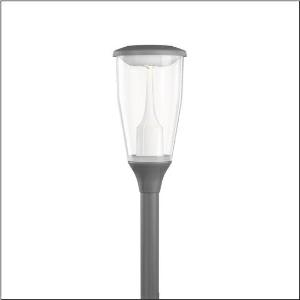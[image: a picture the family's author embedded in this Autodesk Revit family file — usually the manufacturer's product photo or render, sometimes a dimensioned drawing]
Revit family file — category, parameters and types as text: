
# Revit family: dl_11_iq___p1_0a_5xa5575bf14h000022_7e97
name_source: partatom
category: Lighting Fixtures
units: mm (PartAtom-declared; Revit-internal decimal feet)

## family parameters
Cut with Voids When Loaded = No
Host = Face
Light Source = No
Part Type = Normal
Room Calculation Point = No
Round Connector Dimension = Use Diameter
Shared = No

## types (1)
- --- (1 x LED, 1530 lm, 12.9 W, 2200K)
    Apparent Load = 13 VA
    CIE Flux Codes = 34 63 91 95 100
    Color Rendering = 70
    Color Temperature = 2200K
    Default Elevation = 1800 mm
    Description = DL 11 iQ, mast luminaire, Module 540 iQ-SR, primary light control with 3 zone facetted reflector, of plastic, silver coated, highly specular, structured, primary optical cover: cover, of PMMA, transparent, light distribution: P1.0a, light emission: direct distribution, primary light characteristic: asymmetric, installation type: post-top, LED, High Power LED, rated luminous flux: 1.560lm, luminous efficacy: 149lm/W, light colour: 722, colour temperature: 2200K, control: Street-Remote, Auto-Match, Temp-Guard, Lumen-Switch, Night-Set, Smart-Wire, Light-Fading, Desk-Remote (wireless, voltage-free reading and setting of iQ features in the workshop via application-optimized NFC function/RFID function), optimised constant luminous flux control (CLO 2.0), mains connection: 220..240V, AC, 50/60Hz, connection cable pre-assembled, cable length: 5,5m, wiring characteristics: H07RN-F, 5-core, 1.5mm², start of lifetime: 13W, end of service life: 13W, reduction: 5W, luminaire housing, upper part, of diecast aluminium, coated, Siteco® metallic grey (DB 702S), spigot size: 76mm (post-top), post-top mast mounting element, of diecast aluminium, coated, Siteco® metallic grey (DB 702S), Module 540 iQ-SR, traffic white (RAL 9016), equipment: standard, protection rating (complete): IP66, insulation class (complete): insulation class II (safety insulation), certification: CE, ENEC, ENEC+, VDE, packaging unit: 1 piece

Light Distribution: P1.0a
    Height = 665 mm
    Lamp = 1 x LED
    Lamp Light Flux = 1530 lm
    Lamp Power = 12.9 W
    Lamp count = 1
    Length = 334 mm
    Luminous efficacy = 119 lm/W
    Manufacturer = Siteco
    ModVariant = No
    Model = 5XA5575BF14H000022
    Number of Poles = 1
    OnlyDefault = Yes
    Power Factor = 1
    Product Name = DL 11 iQ | P1.0a
    Product group = mast luminaire | pylon top
    ProductGroupID = 6100
    Protection Class = Protection class II
    Protection Degree = IP 66
    RLX_Detail_Level = 1
    RLX_Emergency_Light_Flux = 0 lm
    RLX_Emergency_Type = 0
    RLX_Emergency_Type_DB = No
    RlxData = <blob elided: 103861 chars, md5=cca22863>
    Socket = socket
    Standby Power = 0 W
    System Light Flux = 1530 lm
    System Power = 13 W
    Type Comments = factory setting: luminous flux: 100 % | dim-lin: 254 | 516 mA
    Type Image = l_1258354.jpg
    URL = http://relux.com
    VarID = @adj_024181
    Voltage = 0 V
    Weight = 0.00 kg
    Width = 0 mm  [stored 0 ft]

note: [stored X ft] marks values corroborated as IEEE doubles in the binary element streams (Revit-internal decimal feet)

## geometry (parser evidence)
native form markers: Blend x4, Sweep x12
no freeform markers — native parametric forms only
